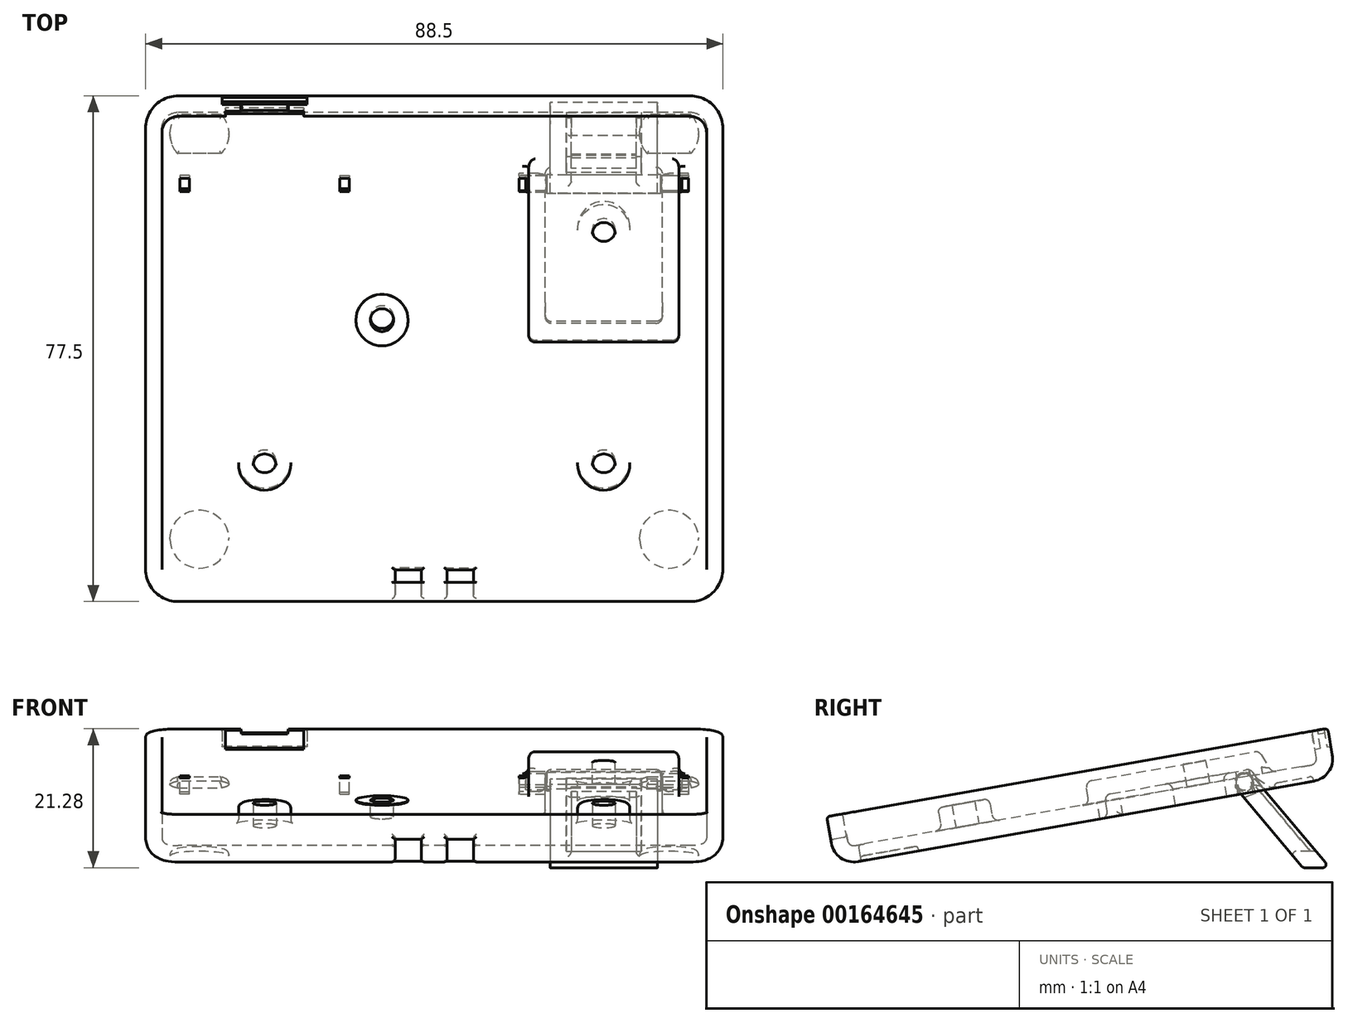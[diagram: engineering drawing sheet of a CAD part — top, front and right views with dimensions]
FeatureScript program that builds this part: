
annotation { "Feature Type Name" : "Feature", "Feature Type Description" : "" }
export const myFeature = defineFeature(function(context is Context, id is Id, definition is map)
    precondition{}
    {
        {
            var Q0;
            Q0=qCreatedBy(makeId("Top.planeOp"),FACE);
            var sketch = newSketch(context, id + "F0", { "sketchPlane" : qUnion([Q0])});
            skLineSegment(sketch, "E0.bottom", {"start": v(-44.25, 39) * mm, "end": v(44.25, 39) * mm});
            skLineSegment(sketch, "E0.top", {"start": v(-44.25, -39) * mm, "end": v(44.25, -39) * mm});
            skLineSegment(sketch, "E0.left", {"start": v(-44.25, 39) * mm, "end": v(-44.25, -39) * mm});
            skLineSegment(sketch, "E0.right", {"start": v(44.25, 39) * mm, "end": v(44.25, -39) * mm});
            skPoint(sketch, "E1", {"position": v(0, -39) * mm});
            skSolve(sketch);
        }
        {
            var Q0;
            Q0=qSketchRegion(id+"F0",true);
            extrude(context, id + "F1", {"entities" : qUnion([Q0]), "depth" : 7.6 * mm});
        }
        {
            var Q0;
            Q0=makeQuery(id+"F1.opExtrude","SWEPT_EDGE",EDGE,{"disambiguationData":[OSD([sQuery(id+"F0.wireOp",EDGE,"E0.top"),sQuery(id+"F0.wireOp",EDGE,"E0.left")])]});
            var Q1;
            Q1=makeQuery(id+"F1.opExtrude","SWEPT_EDGE",EDGE,{"disambiguationData":[OSD([sQuery(id+"F0.wireOp",EDGE,"E0.bottom"),sQuery(id+"F0.wireOp",EDGE,"E0.left")])]});
            var Q2;
            Q2=makeQuery(id+"F1.opExtrude","SWEPT_EDGE",EDGE,{"disambiguationData":[OSD([sQuery(id+"F0.wireOp",EDGE,"E0.top"),sQuery(id+"F0.wireOp",EDGE,"E0.right")])]});
            var Q3;
            Q3=makeQuery(id+"F1.opExtrude","SWEPT_EDGE",EDGE,{"disambiguationData":[OSD([sQuery(id+"F0.wireOp",EDGE,"E0.bottom"),sQuery(id+"F0.wireOp",EDGE,"E0.right")])]});
            fillet(context, id + "F2", {"entities" : qUnion([Q0, Q1, Q2, Q3]), "radius" : 5 * mm, "tangentPropagation" : true, "allowEdgeOverflow" : false});
        }
        {
            assignVariable(context, id + "F3", {"name" : "Thickness", "anyValue" : 2.5});
        }
        {
            var Q0;
            Q0=makeQuery(id+"F1.opExtrude","CAP_FACE",FACE,{"disambiguationData":[OSD([sQuery(id+"F0.wireOp",EDGE,"E0.bottom"),sQuery(id+"F0.wireOp",EDGE,"E0.top"),sQuery(id+"F0.wireOp",EDGE,"E0.left"),sQuery(id+"F0.wireOp",EDGE,"E0.right")])],"isStart":false});
            shell(context, id + "F4", {"entities" : qUnion([Q0]), "thickness" : (getVariable(context, 'Thickness')) * mm});
        }
        {
            var Q0;
            Q0=makeQuery(id+"F4.opShell","OFFSET_FACE",FACE,{"disambiguationData":[OSD([sQuery(id+"F0.wireOp",EDGE,"E0.bottom"),sQuery(id+"F0.wireOp",EDGE,"E0.top"),sQuery(id+"F0.wireOp",EDGE,"E0.left"),sQuery(id+"F0.wireOp",EDGE,"E0.right")])]});
            var sketch = newSketch(context, id + "F5", { "sketchPlane" : qUnion([Q0])});
            skCircle(sketch, "E2", {"center": v(-26, -18) * mm, "radius": 4 * mm});
            skCircle(sketch, "E3.0.1.0", {"center": v(-26, 18) * mm, "radius": 4 * mm, "construction": true});
            skCircle(sketch, "E3.1.0.0", {"center": v(26, -18) * mm, "radius": 4 * mm});
            skCircle(sketch, "E3.1.1.0", {"center": v(26, 18) * mm, "radius": 4 * mm, "construction": true});
            skLineSegment(sketch, "E3.direction1", {"start": v(-26, -18) * mm, "end": v(26, -18) * mm, "construction": true});
            skLineSegment(sketch, "E3.direction2", {"start": v(-26, -18) * mm, "end": v(-26, 18) * mm, "construction": true});
            skSolve(sketch);
        }
        {
            var Q0;
            Q0=qSketchRegion(id+"F5",true);
            extrude(context, id + "F6", {"entities" : qUnion([Q0]), "operationType" : NewBodyOperationType.ADD, "depth" : 3.5 * mm});
        }
        {
            var Q0;
            Q0=makeQuery(id+"F5.imprint","IMPRINT",FACE,{"disambiguationData":[TD([[makeQuery(id+"F5.imprint","IMPRINT",EDGE,{"derivedFrom":sQuery(id+"F5.wireOp",EDGE,"E2")}),-1.0]])]});
            var sketch = newSketch(context, id + "F7", { "sketchPlane" : qUnion([Q0])});
            skCircle(sketch, "E4", {"center": v(-26, -18) * mm, "radius": 1.77 * mm});
            skCircle(sketch, "E5.0.1.0", {"center": v(-26, 18) * mm, "radius": 1.77 * mm});
            skCircle(sketch, "E5.1.0.0", {"center": v(26, -18) * mm, "radius": 1.77 * mm});
            skCircle(sketch, "E5.1.1.0", {"center": v(26, 18) * mm, "radius": 1.77 * mm});
            skLineSegment(sketch, "E5.direction1", {"start": v(-26, -18) * mm, "end": v(26, -18) * mm, "construction": true});
            skLineSegment(sketch, "E5.direction2", {"start": v(-26, -18) * mm, "end": v(-26, 18) * mm, "construction": true});
            skSolve(sketch);
        }
        {
            var Q0;
            Q0=qSketchRegion(id+"F7",true);
            extrude(context, id + "F8", {"entities" : qUnion([Q0]), "operationType" : NewBodyOperationType.REMOVE, "depth" : 25 * mm});
        }
        {
            var Q0;
            Q0=makeQuery(id+"F6.opExtrude","CAP_EDGE",EDGE,{"disambiguationData":[OSD([sQuery(id+"F5.wireOp",EDGE,"E3.0.1.0")])],"isStart":false});
            var Q1;
            Q1=makeQuery(id+"F6.opExtrude","CAP_EDGE",EDGE,{"disambiguationData":[OSD([sQuery(id+"F5.wireOp",EDGE,"E2")])],"isStart":false});
            var Q2;
            Q2=makeQuery(id+"F6.opExtrude","CAP_EDGE",EDGE,{"disambiguationData":[OSD([sQuery(id+"F5.wireOp",EDGE,"E3.1.1.0")])],"isStart":false});
            var Q3;
            Q3=makeQuery(id+"F6.opExtrude","CAP_EDGE",EDGE,{"disambiguationData":[OSD([sQuery(id+"F5.wireOp",EDGE,"E3.1.0.0")])],"isStart":false});
            fillet(context, id + "F9", {"entities" : qUnion([Q0, Q1, Q2, Q3]), "radius" : 0.8 * mm, "tangentPropagation" : true, "allowEdgeOverflow" : false});
        }
        {
            var Q0;
            Q0=makeQuery(id+"F4.opShell","OFFSET_FACE",FACE,{"disambiguationData":[OSD([sQuery(id+"F0.wireOp",EDGE,"E0.bottom"),sQuery(id+"F0.wireOp",EDGE,"E0.top"),sQuery(id+"F0.wireOp",EDGE,"E0.left"),sQuery(id+"F0.wireOp",EDGE,"E0.right")])]});
            fillet(context, id + "F10", {"entities" : qUnion([Q0]), "radius" : 1 * mm, "tangentPropagation" : true, "allowEdgeOverflow" : false});
        }
        {
            var Q0;
            Q0=makeQuery(id+"F1.opExtrude","CAP_FACE",FACE,{"disambiguationData":[OSD([sQuery(id+"F0.wireOp",EDGE,"E0.bottom"),sQuery(id+"F0.wireOp",EDGE,"E0.top"),sQuery(id+"F0.wireOp",EDGE,"E0.left"),sQuery(id+"F0.wireOp",EDGE,"E0.right")])],"isStart":true});
            fillet(context, id + "F11", {"entities" : qUnion([Q0]), "radius" : 3.5 * mm, "tangentPropagation" : true, "allowEdgeOverflow" : false});
        }
        {
            var Q0;
            Q0=makeQuery(id+"F1.opExtrude","CAP_FACE",FACE,{"disambiguationData":[OSD([sQuery(id+"F0.wireOp",EDGE,"E0.bottom"),sQuery(id+"F0.wireOp",EDGE,"E0.top"),sQuery(id+"F0.wireOp",EDGE,"E0.left"),sQuery(id+"F0.wireOp",EDGE,"E0.right")])],"isStart":true});
            var sketch = newSketch(context, id + "F12", { "sketchPlane" : qUnion([Q0])});
            skLineSegment(sketch, "E6", {"start": v(0, 29.34) * mm, "end": v(0, 8.5) * mm, "construction": true});
            skCircle(sketch, "E7", {"center": v(-36, 30.5) * mm, "radius": 4.5 * mm});
            skCircle(sketch, "E8.MirrorC", {"center": v(36, 30.5) * mm, "radius": 4.5 * mm});
            skLineSegment(sketch, "E9.direction1", {"start": v(-36, 30.5) * mm, "end": v(-15, 30.5) * mm, "construction": true});
            skCircle(sketch, "E10.0.1.0", {"center": v(-36, -32.5) * mm, "radius": 4.5 * mm, "construction": true});
            skLineSegment(sketch, "E10.direction2", {"start": v(-36, 30.5) * mm, "end": v(-36, -32.5) * mm, "construction": true});
            skCircle(sketch, "E11.0.1.0", {"center": v(36, -33.5) * mm, "radius": 4.5 * mm, "construction": true});
            skLineSegment(sketch, "E11.direction1", {"start": v(36, 30.5) * mm, "end": v(61, 30.5) * mm, "construction": true});
            skLineSegment(sketch, "E11.direction2", {"start": v(36, 30.5) * mm, "end": v(36, -33.5) * mm, "construction": true});
            skLineSegment(sketch, "E12", {"start": v(-39.35, -29.5) * mm, "end": v(-32.65, -29.5) * mm});
            skLineSegment(sketch, "E13", {"start": v(-32.65, -35.5) * mm, "end": v(-39.35, -35.5) * mm});
            skLineSegment(sketch, "E14", {"start": v(-36.31, -32.5) * mm, "end": v(-36, -32.5) * mm, "construction": true});
            skArc(sketch, "E15", {"start": v(-32.65, -35.5) * mm, "mid": v(-31.5, -32.5) * mm, "end": v(-32.65, -29.5) * mm});
            skArc(sketch, "E16", {"start": v(-39.35, -29.5) * mm, "mid": v(-40.5, -32.5) * mm, "end": v(-39.35, -35.5) * mm});
            skLineSegment(sketch, "E17.1.0.0", {"start": v(39.35, -35.5) * mm, "end": v(32.65, -35.5) * mm});
            skArc(sketch, "E17.1.0.1", {"start": v(39.35, -35.5) * mm, "mid": v(40.5, -32.5) * mm, "end": v(39.35, -29.5) * mm});
            skArc(sketch, "E17.1.0.2", {"start": v(32.65, -29.5) * mm, "mid": v(31.5, -32.5) * mm, "end": v(32.65, -35.5) * mm});
            skLineSegment(sketch, "E17.1.0.3", {"start": v(32.65, -29.5) * mm, "end": v(39.35, -29.5) * mm});
            skLineSegment(sketch, "E17.direction1", {"start": v(-39.35, -35.5) * mm, "end": v(32.65, -35.5) * mm, "construction": true});
            skSolve(sketch);
        }
        {
            var Q0;
            Q0=makeQuery(id+"F1.opExtrude","CAP_FACE",FACE,{"disambiguationData":[OSD([sQuery(id+"F0.wireOp",EDGE,"E0.bottom"),sQuery(id+"F0.wireOp",EDGE,"E0.top"),sQuery(id+"F0.wireOp",EDGE,"E0.left"),sQuery(id+"F0.wireOp",EDGE,"E0.right")])],"isStart":false});
            fillet(context, id + "F13", {"entities" : qUnion([Q0]), "radius" : 0.5 * mm, "tangentPropagation" : true, "allowEdgeOverflow" : false});
        }
        {
            var Q0;
            Q0=qCreatedBy(makeId("Top.planeOp"),FACE);
            var sketch = newSketch(context, id + "F14", { "sketchPlane" : qUnion([Q0])});
            skLineSegment(sketch, "E18", {"start": v(-15.25, 0) * mm, "end": v(18.86, 0) * mm});
            skSolve(sketch);
        }
        {
            assignVariable(context, id + "F15", {"name" : "FootWidth", "anyValue" : 23});
        }
        {
            var Q0;
            Q0=qCreatedBy(makeId("Right.planeOp"),FACE);
            cPlane(context, id + "F16", {"entities" : qUnion([Q0]), "cplaneType" : CPlaneType.OFFSET, "offset" : 26 * mm, "width" : 150 * mm, "height" : 150 * mm});
        }
        {
            var Q0;
            Q0=qCreatedBy(id+"F16.planeOp",FACE);
            var sketch = newSketch(context, id + "F17", { "sketchPlane" : qUnion([Q0])});
            skLineSegment(sketch, "E19", {"start": v(1, 6) * mm, "end": v(28, 6) * mm});
            skLineSegment(sketch, "E20", {"start": v(28, 6) * mm, "end": v(30.42, 0) * mm});
            skLineSegment(sketch, "E21", {"start": v(30.42, 0) * mm, "end": v(1, 0) * mm});
            skLineSegment(sketch, "E22", {"start": v(1, 0) * mm, "end": v(1, 6) * mm});
            skSolve(sketch);
        }
        {
            var Q0;
            Q0=qSketchRegion(id+"F17",true);
            extrude(context, id + "F18", {"entities" : qUnion([Q0]), "operationType" : NewBodyOperationType.ADD, "endBound" : BoundingType.SYMMETRIC, "depth" : (getVariable(context, 'FootWidth')) * mm});
        }
        {
            var Q0;
            Q0=qCreatedBy(id+"F16.planeOp",FACE);
            var sketch = newSketch(context, id + "F19", { "sketchPlane" : qUnion([Q0])});
            skLineSegment(sketch, "E23.0", {"start": v(26.31, 3.5) * mm, "end": v(27.73, 0) * mm});
            skLineSegment(sketch, "E23.1", {"start": v(3.5, 3.5) * mm, "end": v(26.31, 3.5) * mm});
            skLineSegment(sketch, "E23.2", {"start": v(3.5, 0) * mm, "end": v(3.5, 3.5) * mm});
            skLineSegment(sketch, "E24", {"start": v(3.5, 0) * mm, "end": v(27.73, 0) * mm});
            skSolve(sketch);
        }
        {
            var Q0;
            Q0=qSketchRegion(id+"F19",true);
            extrude(context, id + "F20", {"entities" : qUnion([Q0]), "operationType" : NewBodyOperationType.REMOVE, "endBound" : BoundingType.SYMMETRIC, "oppositeDirection" : true, "depth" : (getVariable(context, 'FootWidth') - 2.5 * 2) * mm});
        }
        {
            var Q0;
            Q0=qSketchRegion(id+"F12",true);
            extrude(context, id + "F21", {"entities" : qUnion([Q0]), "operationType" : NewBodyOperationType.REMOVE, "oppositeDirection" : true, "depth" : 0.75 * mm});
        }
        {
            var Q0;
            Q0=makeQuery(id+"F21.boolean.opBoolean","COPY",EDGE,{"derivedFrom":makeQuery(id+"F21.opExtrude","CAP_EDGE",EDGE,{"disambiguationData":[OSD([sQuery(id+"F12.wireOp",EDGE,"E7")])],"isStart":false})});
            var Q1;
            Q1=makeQuery(id+"F21.boolean.opBoolean","COPY",EDGE,{"derivedFrom":makeQuery(id+"F21.opExtrude","CAP_EDGE",EDGE,{"disambiguationData":[OSD([sQuery(id+"F12.wireOp",EDGE,"E8.MirrorC")])],"isStart":false})});
            var Q2;
            Q2=makeQuery(id+"F21.boolean.opBoolean","COPY",EDGE,{"derivedFrom":makeQuery(id+"F21.opExtrude","CAP_EDGE",EDGE,{"disambiguationData":[OSD([sQuery(id+"F12.wireOp",EDGE,"E16")])],"isStart":false})});
            var Q3;
            Q3=makeQuery(id+"F21.boolean.opBoolean","COPY",EDGE,{"derivedFrom":makeQuery(id+"F21.opExtrude","CAP_EDGE",EDGE,{"disambiguationData":[OSD([sQuery(id+"F12.wireOp",EDGE,"E12")])],"isStart":false})});
            var Q4;
            Q4=makeQuery(id+"F21.boolean.opBoolean","COPY",EDGE,{"derivedFrom":makeQuery(id+"F21.opExtrude","CAP_EDGE",EDGE,{"disambiguationData":[OSD([sQuery(id+"F12.wireOp",EDGE,"E15")])],"isStart":false})});
            var Q5;
            Q5=makeQuery(id+"F21.boolean.opBoolean","COPY",EDGE,{"derivedFrom":makeQuery(id+"F21.opExtrude","CAP_EDGE",EDGE,{"disambiguationData":[OSD([sQuery(id+"F12.wireOp",EDGE,"E13")])],"isStart":false})});
            var Q6;
            Q6=makeQuery(id+"F21.boolean.opBoolean","COPY",EDGE,{"derivedFrom":makeQuery(id+"F21.opExtrude","CAP_EDGE",EDGE,{"disambiguationData":[OSD([sQuery(id+"F12.wireOp",EDGE,"E17.1.0.2")])],"isStart":false})});
            var Q7;
            Q7=makeQuery(id+"F21.boolean.opBoolean","COPY",EDGE,{"derivedFrom":makeQuery(id+"F21.opExtrude","CAP_EDGE",EDGE,{"disambiguationData":[OSD([sQuery(id+"F12.wireOp",EDGE,"E17.1.0.3")])],"isStart":false})});
            var Q8;
            Q8=makeQuery(id+"F21.boolean.opBoolean","COPY",EDGE,{"derivedFrom":makeQuery(id+"F21.opExtrude","CAP_EDGE",EDGE,{"disambiguationData":[OSD([sQuery(id+"F12.wireOp",EDGE,"E17.1.0.1")])],"isStart":false})});
            var Q9;
            Q9=makeQuery(id+"F21.boolean.opBoolean","COPY",EDGE,{"derivedFrom":makeQuery(id+"F21.opExtrude","CAP_EDGE",EDGE,{"disambiguationData":[OSD([sQuery(id+"F12.wireOp",EDGE,"E17.1.0.0")])],"isStart":false})});
            fillet(context, id + "F22", {"entities" : qUnion([Q0, Q1, Q2, Q3, Q4, Q5, Q6, Q7, Q8, Q9]), "radius" : 0.5 * mm, "tangentPropagation" : true, "allowEdgeOverflow" : false});
        }
        {
            var Q0;
            Q0=makeQuery(id+"F9l8tkFQPLfUdVu_1.1.F18.opExtrude","SWEPT_FACE",FACE,{"disambiguationData":[OSD([sQuery(id+"F17.wireOp",EDGE,"E19")])]});
            var Q1;
            Q1=makeQuery(id+"F9l8tkFQPLfUdVu_1.1.F20.boolean.opBoolean","COPY",FACE,{"derivedFrom":makeQuery(id+"F9l8tkFQPLfUdVu_1.1.F20.opExtrude","SWEPT_FACE",FACE,{"disambiguationData":[OSD([sQuery(id+"F19.wireOp",EDGE,"E23.1")])]})});
            var Q2;
            Q2=makeQuery(id+"F20.boolean.opBoolean","COPY",FACE,{"derivedFrom":makeQuery(id+"F20.opExtrude","SWEPT_FACE",FACE,{"disambiguationData":[OSD([sQuery(id+"F19.wireOp",EDGE,"E23.1")])]})});
            var Q3;
            Q3=makeQuery(id+"F9l8tkFQPLfUdVu_1.1.F18.opExtrude","SWEPT_FACE",FACE,{"disambiguationData":[OSD([sQuery(id+"F17.wireOp",EDGE,"E22")])]});
            var Q4;
            Q4=makeQuery(id+"F9l8tkFQPLfUdVu_1.1.F18.opExtrude","SWEPT_FACE",FACE,{"disambiguationData":[OSD([sQuery(id+"F17.wireOp",EDGE,"E20")])]});
            var Q5;
            Q5=makeQuery(id+"F18.opExtrude","SWEPT_FACE",FACE,{"disambiguationData":[OSD([sQuery(id+"F17.wireOp",EDGE,"E22")])]});
            var Q6;
            Q6=makeQuery(id+"F18.opExtrude","SWEPT_FACE",FACE,{"disambiguationData":[OSD([sQuery(id+"F17.wireOp",EDGE,"E20")])]});
            var Q7;
            Q7=makeQuery(id+"F9l8tkFQPLfUdVu_1.1.F20.boolean.opBoolean","COPY",FACE,{"derivedFrom":makeQuery(id+"F9l8tkFQPLfUdVu_1.1.F20.opExtrude","SWEPT_FACE",FACE,{"disambiguationData":[OSD([sQuery(id+"F19.wireOp",EDGE,"E23.2")])]})});
            var Q8;
            Q8=makeQuery(id+"F9l8tkFQPLfUdVu_1.1.F20.boolean.opBoolean","COPY",FACE,{"derivedFrom":makeQuery(id+"F9l8tkFQPLfUdVu_1.1.F20.opExtrude","SWEPT_FACE",FACE,{"disambiguationData":[OSD([sQuery(id+"F19.wireOp",EDGE,"E23.0")])]})});
            var Q9;
            Q9=makeQuery(id+"F20.boolean.opBoolean","COPY",FACE,{"derivedFrom":makeQuery(id+"F20.opExtrude","SWEPT_FACE",FACE,{"disambiguationData":[OSD([sQuery(id+"F19.wireOp",EDGE,"E23.2")])]})});
            var Q10;
            Q10=makeQuery(id+"F20.boolean.opBoolean","COPY",FACE,{"derivedFrom":makeQuery(id+"F20.opExtrude","SWEPT_FACE",FACE,{"disambiguationData":[OSD([sQuery(id+"F19.wireOp",EDGE,"E23.0")])]})});
            var Q11;
            Q11=makeQuery(id+"F18.opExtrude","CAP_FACE",FACE,{"disambiguationData":[OSD([sQuery(id+"F17.wireOp",EDGE,"E19"),sQuery(id+"F17.wireOp",EDGE,"E20"),sQuery(id+"F17.wireOp",EDGE,"E21"),sQuery(id+"F17.wireOp",EDGE,"E22")])],"isStart":false});
            var Q12;
            Q12=makeQuery(id+"F18.opExtrude","CAP_FACE",FACE,{"disambiguationData":[OSD([sQuery(id+"F17.wireOp",EDGE,"E19"),sQuery(id+"F17.wireOp",EDGE,"E20"),sQuery(id+"F17.wireOp",EDGE,"E21"),sQuery(id+"F17.wireOp",EDGE,"E22")])],"isStart":true});
            fillet(context, id + "F23", {"entities" : qUnion([Q0, Q1, Q2, Q3, Q4, Q5, Q6, Q7, Q8, Q9, Q10, Q11, Q12]), "radius" : 1 * mm, "tangentPropagation" : true, "allowEdgeOverflow" : false});
        }
        {
            var Q0;
            Q0=makeQuery(id+"F18.opExtrude","SWEPT_FACE",FACE,{"disambiguationData":[OSD([sQuery(id+"F17.wireOp",EDGE,"E19")])]});
            var sketch = newSketch(context, id + "F24", { "sketchPlane" : qUnion([Q0])});
            skCircle(sketch, "E25.0", {"center": v(26, 18) * mm, "radius": 4 * mm});
            skSolve(sketch);
        }
        {
            var Q0;
            Q0=qSketchRegion(id+"F24",true);
            var Q1;
            Q1=makeQuery(id+"F1.opExtrude","CAP_FACE",FACE,{"disambiguationData":[OSD([sQuery(id+"F0.wireOp",EDGE,"E0.bottom"),sQuery(id+"F0.wireOp",EDGE,"E0.top"),sQuery(id+"F0.wireOp",EDGE,"E0.left"),sQuery(id+"F0.wireOp",EDGE,"E0.right")])],"isStart":true});
            extrude(context, id + "F25", {"entities" : qUnion([Q0]), "operationType" : NewBodyOperationType.ADD, "endBound" : BoundingType.UP_TO_SURFACE, "oppositeDirection" : true, "endBoundEntityFace" : qUnion([Q1]), "depth" : 25 * mm});
        }
        {
            var Q0;
            Q0=makeQuery(id+"F18.opExtrude","SWEPT_FACE",FACE,{"disambiguationData":[OSD([sQuery(id+"F17.wireOp",EDGE,"E19")])]});
            var sketch = newSketch(context, id + "F26", { "sketchPlane" : qUnion([Q0])});
            skCircle(sketch, "E26.0", {"center": v(26, 18) * mm, "radius": 1.77 * mm});
            skSolve(sketch);
        }
        {
            var Q0;
            Q0=qSketchRegion(id+"F26",true);
            extrude(context, id + "F27", {"entities" : qUnion([Q0]), "operationType" : NewBodyOperationType.REMOVE, "oppositeDirection" : true, "depth" : 3.5 * mm});
        }
        {
            var Q0;
            Q0=makeQuery(id+"F25.opExtrude","TWEAK_EDGE",EDGE,{"derivedFrom":[makeQuery(id+"F1.opExtrude","CAP_FACE",FACE,{"disambiguationData":[OSD([sQuery(id+"F0.wireOp",EDGE,"E0.bottom"),sQuery(id+"F0.wireOp",EDGE,"E0.top"),sQuery(id+"F0.wireOp",EDGE,"E0.left"),sQuery(id+"F0.wireOp",EDGE,"E0.right")])],"isStart":true}),makeQuery(id+"F24.imprint","IMPRINT",EDGE,{"derivedFrom":sQuery(id+"F24.wireOp",EDGE,"E25.0")})]});
            var Q1;
            Q1=makeQuery(id+"F25.boolean.opBoolean","INTERSECT",EDGE,{"derivedFrom":[makeQuery(id+"F20.boolean.opBoolean","COPY",FACE,{"derivedFrom":makeQuery(id+"F20.opExtrude","SWEPT_FACE",FACE,{"disambiguationData":[OSD([sQuery(id+"F19.wireOp",EDGE,"E23.1")])]})}),makeQuery(id+"F25.opExtrude","SWEPT_FACE",FACE,{"disambiguationData":[OSD([sQuery(id+"F24.wireOp",EDGE,"E25.0")])]})]});
            fillet(context, id + "F28", {"entities" : qUnion([Q0, Q1]), "radius" : 1 * mm, "tangentPropagation" : true, "allowEdgeOverflow" : false});
        }
        {
            var Q0;
            Q0=qCreatedBy(id+"F16.planeOp",FACE);
            var sketch = newSketch(context, id + "F29", { "sketchPlane" : qUnion([Q0])});
            skArc(sketch, "E27", {"start": v(26.22, 1.25) * mm, "mid": v(25, 3) * mm, "end": v(23.78, 1.25) * mm});
            skLineSegment(sketch, "E28", {"start": v(23.65, 0) * mm, "end": v(26.35, 0) * mm});
            skLineSegment(sketch, "E29", {"start": v(23.78, 1.25) * mm, "end": v(23.85, 1.06) * mm});
            skLineSegment(sketch, "E30", {"start": v(23.85, 1.06) * mm, "end": v(23.65, 0) * mm});
            skLineSegment(sketch, "E31", {"start": v(26.22, 1.25) * mm, "end": v(26.15, 1.06) * mm});
            skLineSegment(sketch, "E32", {"start": v(26.15, 1.06) * mm, "end": v(26.35, 0) * mm});
            skLineSegment(sketch, "E33", {"start": v(25, 1.7) * mm, "end": v(25, 0.9) * mm, "construction": true});
            skPoint(sketch, "E34.0", {"position": v(1, 0) * mm});
            skSolve(sketch);
        }
        {
            var Q0;
            Q0=qSketchRegion(id+"F29",true);
            extrude(context, id + "F30", {"entities" : qUnion([Q0]), "operationType" : NewBodyOperationType.REMOVE, "endBound" : BoundingType.SYMMETRIC, "depth" : (getVariable(context, 'FootWidth') + 3) * mm});
        }
        {
            var Q0;
            Q0=makeQuery(id+"F1.opExtrude","SWEPT_BODY",BODY,{"disambiguationData":[OSD([sQuery(id+"F0.wireOp",EDGE,"E0.bottom"),sQuery(id+"F0.wireOp",EDGE,"E0.top"),sQuery(id+"F0.wireOp",EDGE,"E0.left"),sQuery(id+"F0.wireOp",EDGE,"E0.right")])]});
            var Q1;
            Q1=sQuery(id+"F14.wireOp",EDGE,"E18");
            transform(context, id + "F31", {"entities" : qUnion([Q0]), "transformType" : TransformType.ROTATION, "transformAxis" : qUnion([Q1]), "angle" : 10 * degree, "makeCopy" : false});
        }
        {
            var Q0;
            Q0=qCreatedBy(id+"F16.planeOp",FACE);
            var sketch = newSketch(context, id + "F32", { "sketchPlane" : qUnion([Q0])});
            skLineSegment(sketch, "E35", {"start": v(-33.48, -7.1) * mm, "end": v(29.13, -7.1) * mm, "construction": true});
            skLineSegment(sketch, "E36", {"start": v(29.13, -7.1) * mm, "end": v(29.13, 7.53) * mm, "construction": true});
            skLineSegment(sketch, "E37", {"start": v(23.12, 5.69) * mm, "end": v(25.51, 6.42) * mm});
            skCircle(sketch, "E38", {"center": v(24.32, 6.06) * mm, "radius": 1.25 * mm, "construction": true});
            skLineSegment(sketch, "E39.0", {"start": v(-26.23, -3.86) * mm, "end": v(-34.1, -5.25) * mm, "construction": true});
            skLineSegment(sketch, "E40.0", {"start": v(-27.36, -6.1) * mm, "end": v(-35.24, -7.48) * mm, "construction": true});
            skLineSegment(sketch, "E41", {"start": v(22.63, 5.54) * mm, "end": v(33.3, -7.1) * mm});
            skLineSegment(sketch, "E42", {"start": v(25.9, 6.54) * mm, "end": v(37.42, -7.1) * mm});
            skLineSegment(sketch, "E43", {"start": v(22.63, 5.54) * mm, "end": v(23.12, 5.69) * mm});
            skLineSegment(sketch, "E44", {"start": v(25.9, 6.54) * mm, "end": v(25.51, 6.42) * mm});
            skLineSegment(sketch, "E45", {"start": v(37.42, -7.1) * mm, "end": v(33.3, -7.1) * mm});
            skArc(sketch, "E46.0", {"start": v(28.3, 7.6) * mm, "mid": v(28.39, 7.4) * mm, "end": v(28.45, 7.19) * mm});
            skSolve(sketch);
        }
        {
            var Q0;
            Q0=qSketchRegion(id+"F32",true);
            extrude(context, id + "F33", {"entities" : qUnion([Q0]), "endBound" : BoundingType.SYMMETRIC, "depth" : 16.5 * mm});
        }
        {
            var Q0;
            Q0=qCreatedBy(id+"F16.planeOp",FACE);
            var sketch = newSketch(context, id + "F34", { "sketchPlane" : qUnion([Q0])});
            skCircle(sketch, "E47.0", {"center": v(24.32, 6.06) * mm, "radius": 1.25 * mm});
            skSolve(sketch);
        }
        {
            var Q0;
            Q0=makeQuery(id+"F4.opShell","OFFSET_FACE",FACE,{"disambiguationData":[OSD([sQuery(id+"F0.wireOp",EDGE,"E0.bottom"),sQuery(id+"F0.wireOp",EDGE,"E0.top"),sQuery(id+"F0.wireOp",EDGE,"E0.left"),sQuery(id+"F0.wireOp",EDGE,"E0.right")])]});
            var sketch = newSketch(context, id + "F35", { "sketchPlane" : qUnion([Q0])});
            skLineSegment(sketch, "E48.bottom", {"start": v(-39, 26.02) * mm, "end": v(-37.5, 26.02) * mm});
            skLineSegment(sketch, "E48.top", {"start": v(-39, 23.98) * mm, "end": v(-37.5, 23.98) * mm});
            skLineSegment(sketch, "E48.left", {"start": v(-39, 26.02) * mm, "end": v(-39, 23.98) * mm});
            skLineSegment(sketch, "E48.right", {"start": v(-37.5, 26.02) * mm, "end": v(-37.5, 23.98) * mm});
            skLineSegment(sketch, "E49.MirrorCS", {"start": v(-13, 23.98) * mm, "end": v(-14.5, 23.98) * mm});
            skLineSegment(sketch, "E50.MirrorCS", {"start": v(-13, 26.02) * mm, "end": v(-14.5, 26.02) * mm});
            skLineSegment(sketch, "E51.MirrorCS", {"start": v(-13, 26.02) * mm, "end": v(-13, 23.98) * mm});
            skLineSegment(sketch, "E52.MirrorCS", {"start": v(-14.5, 26.02) * mm, "end": v(-14.5, 23.98) * mm});
            skLineSegment(sketch, "E53", {"start": v(0, 27.5) * mm, "end": v(0, 11.46) * mm, "construction": true});
            skLineSegment(sketch, "E54.MirrorCS", {"start": v(39, 26.02) * mm, "end": v(37.5, 26.02) * mm});
            skLineSegment(sketch, "E55.MirrorCS", {"start": v(39, 23.98) * mm, "end": v(37.5, 23.98) * mm});
            skLineSegment(sketch, "E56.MirrorCS", {"start": v(13, 26.02) * mm, "end": v(14.5, 26.02) * mm});
            skLineSegment(sketch, "E57.MirrorCS", {"start": v(13, 23.98) * mm, "end": v(14.5, 23.98) * mm});
            skLineSegment(sketch, "E58.MirrorCS", {"start": v(14.5, 26.02) * mm, "end": v(14.5, 23.98) * mm});
            skLineSegment(sketch, "E59.MirrorCS", {"start": v(39, 26.02) * mm, "end": v(39, 23.98) * mm});
            skLineSegment(sketch, "E60.MirrorCS", {"start": v(13, 26.02) * mm, "end": v(13, 23.98) * mm});
            skLineSegment(sketch, "E61.MirrorCS", {"start": v(37.5, 26.02) * mm, "end": v(37.5, 23.98) * mm});
            skSolve(sketch);
        }
        {
            var Q0;
            Q0=qSketchRegion(id+"F35",true);
            var Q1;
            Q1=makeQuery(id+"F1.opExtrude","CAP_FACE",FACE,{"disambiguationData":[OSD([sQuery(id+"F0.wireOp",EDGE,"E0.bottom"),sQuery(id+"F0.wireOp",EDGE,"E0.top"),sQuery(id+"F0.wireOp",EDGE,"E0.left"),sQuery(id+"F0.wireOp",EDGE,"E0.right")])],"isStart":true});
            extrude(context, id + "F36", {"entities" : qUnion([Q0]), "operationType" : NewBodyOperationType.REMOVE, "endBound" : BoundingType.UP_TO_SURFACE, "oppositeDirection" : true, "endBoundEntityFace" : qUnion([Q1]), "depth" : 25 * mm, "hasSecondDirection" : true, "secondDirectionOppositeDirection" : false, "secondDirectionDepth" : 25 * mm});
        }
        {
            var Q0;
            Q0=qSketchRegion(id+"F34",true);
            extrude(context, id + "F37", {"entities" : qUnion([Q0]), "operationType" : NewBodyOperationType.ADD, "endBound" : BoundingType.SYMMETRIC, "depth" : 24 * mm});
        }
        {
            var Q0;
            Q0=qCreatedBy(id+"F16.planeOp",FACE);
            var sketch = newSketch(context, id + "F38", { "sketchPlane" : qUnion([Q0])});
            skCircle(sketch, "E62.0", {"center": v(24.32, 6.06) * mm, "radius": 1.45 * mm});
            skSolve(sketch);
        }
        {
            var Q0;
            Q0=qSketchRegion(id+"F38",true);
            extrude(context, id + "F39", {"entities" : qUnion([Q0]), "operationType" : NewBodyOperationType.ADD, "endBound" : BoundingType.SYMMETRIC, "depth" : 17.5 * mm});
        }
        {
            var Q0;
            Q0=qCreatedBy(id+"F16.planeOp",FACE);
            var sketch = newSketch(context, id + "F40", { "sketchPlane" : qUnion([Q0])});
            skLineSegment(sketch, "E63", {"start": v(43.2, -4.6) * mm, "end": v(34.46, -4.6) * mm});
            skLineSegment(sketch, "E64", {"start": v(34.46, -4.6) * mm, "end": v(25.79, 5.68) * mm});
            skLineSegment(sketch, "E65", {"start": v(25.79, 5.68) * mm, "end": v(25.67, 6.98) * mm});
            skLineSegment(sketch, "E66", {"start": v(25.67, 6.98) * mm, "end": v(43.2, -4.6) * mm});
            skSolve(sketch);
        }
        {
            var Q0;
            Q0=qSketchRegion(id+"F40",true);
            extrude(context, id + "F41", {"entities" : qUnion([Q0]), "operationType" : NewBodyOperationType.REMOVE, "endBound" : BoundingType.SYMMETRIC, "oppositeDirection" : true, "depth" : (16.5 - 2.5 * 2) * mm});
        }
        {
            var Q0;
            Q0=qCreatedBy(makeId("Top.planeOp"),FACE);
            var Q1;
            Q1=sQuery(id+"F32.wireOp",VERTEX,"E38.center");
            cPlane(context, id + "F42", {"entities" : qUnion([Q0, Q1]), "cplaneType" : CPlaneType.PLANE_POINT, "offset" : 7 * mm, "width" : 150 * mm, "height" : 150 * mm});
        }
        {
            var Q0;
            Q0=qCreatedBy(id+"F42.planeOp",FACE);
            var sketch = newSketch(context, id + "F43", { "sketchPlane" : qUnion([Q0])});
            skLineSegment(sketch, "E67", {"start": v(12.14, 24.32) * mm, "end": v(28.07, 24.32) * mm});
            skSolve(sketch);
        }
        {
            var Q0;
            Q0=qCreatedBy(id+"F16.planeOp",FACE);
            var sketch = newSketch(context, id + "F44", { "sketchPlane" : qUnion([Q0])});
            skLineSegment(sketch, "E68", {"start": v(37.44, -4.6) * mm, "end": v(28.89, -4.6) * mm});
            skLineSegment(sketch, "E69", {"start": v(28.89, -4.6) * mm, "end": v(22.62, 3.07) * mm});
            skLineSegment(sketch, "E70", {"start": v(22.62, 3.07) * mm, "end": v(28.76, 5.3) * mm});
            skLineSegment(sketch, "E71", {"start": v(28.76, 5.3) * mm, "end": v(37.44, -4.6) * mm});
            skSolve(sketch);
        }
        {
            var Q0;
            Q0=qSketchRegion(id+"F44",true);
            extrude(context, id + "F45", {"entities" : qUnion([Q0]), "operationType" : NewBodyOperationType.REMOVE, "endBound" : BoundingType.SYMMETRIC, "oppositeDirection" : true, "depth" : 10 * mm});
        }
        {
            var Q0;
            Q0=makeQuery(id+"F33.opExtrude","SWEPT_EDGE",EDGE,{"disambiguationData":[OSD([sQuery(id+"F32.wireOp",EDGE,"E42"),sQuery(id+"F32.wireOp",EDGE,"lMs646Tl-KVh7-EVDn-IebO-JsbN2g6ax7Xg")])]});
            var Q1;
            Q1=makeQuery(id+"F33.opExtrude","SWEPT_EDGE",EDGE,{"disambiguationData":[OSD([sQuery(id+"F32.wireOp",EDGE,"E41"),sQuery(id+"F32.wireOp",EDGE,"NX3cYOfe-ebx6-K3RK-W4n3-XHnWPqz6DOJI")])]});
            var Q2;
            Q2=makeQuery(id+"F45.boolean.opBoolean","INTERSECT",EDGE,{"derivedFrom":[makeQuery(id+"F33.opExtrude","SWEPT_FACE",FACE,{"disambiguationData":[OSD([sQuery(id+"F32.wireOp",EDGE,"E41")])]}),makeQuery(id+"F45.opExtrude","SWEPT_FACE",FACE,{"disambiguationData":[OSD([sQuery(id+"F44.wireOp",EDGE,"E68")])]})]});
            var Q3;
            Q3=makeQuery(id+"F45.boolean.opBoolean","INTERSECT",EDGE,{"derivedFrom":[makeQuery(id+"F33.opExtrude","SWEPT_FACE",FACE,{"disambiguationData":[OSD([sQuery(id+"F32.wireOp",EDGE,"E41")])]}),makeQuery(id+"F45.opExtrude","CAP_FACE",FACE,{"disambiguationData":[OSD([sQuery(id+"F44.wireOp",EDGE,"E68"),sQuery(id+"F44.wireOp",EDGE,"E69"),sQuery(id+"F44.wireOp",EDGE,"E70"),sQuery(id+"F44.wireOp",EDGE,"E71")])],"isStart":false})]});
            var Q4;
            Q4=makeQuery(id+"F45.boolean.opBoolean","INTERSECT",EDGE,{"derivedFrom":[makeQuery(id+"F33.opExtrude","SWEPT_FACE",FACE,{"disambiguationData":[OSD([sQuery(id+"F32.wireOp",EDGE,"E41")])]}),makeQuery(id+"F45.opExtrude","SWEPT_FACE",FACE,{"disambiguationData":[OSD([sQuery(id+"F44.wireOp",EDGE,"E70")])]})]});
            var Q5;
            Q5=makeQuery(id+"F45.boolean.opBoolean","INTERSECT",EDGE,{"derivedFrom":[makeQuery(id+"F33.opExtrude","SWEPT_FACE",FACE,{"disambiguationData":[OSD([sQuery(id+"F32.wireOp",EDGE,"E41")])]}),makeQuery(id+"F45.opExtrude","CAP_FACE",FACE,{"disambiguationData":[OSD([sQuery(id+"F44.wireOp",EDGE,"E68"),sQuery(id+"F44.wireOp",EDGE,"E69"),sQuery(id+"F44.wireOp",EDGE,"E70"),sQuery(id+"F44.wireOp",EDGE,"E71")])],"isStart":true})]});
            fillet(context, id + "F46", {"entities" : qUnion([Q0, Q1, Q2, Q3, Q4, Q5]), "radius" : 0.5 * mm, "tangentPropagation" : true, "allowEdgeOverflow" : false});
        }
        {
            var Q0;
            Q0=makeQuery(id+"F1.opExtrude","CAP_FACE",FACE,{"disambiguationData":[OSD([sQuery(id+"F0.wireOp",EDGE,"E0.bottom"),sQuery(id+"F0.wireOp",EDGE,"E0.top"),sQuery(id+"F0.wireOp",EDGE,"E0.left"),sQuery(id+"F0.wireOp",EDGE,"E0.right")])],"isStart":true});
            var sketch = newSketch(context, id + "F47", { "sketchPlane" : qUnion([Q0])});
            skLineSegment(sketch, "E72", {"start": v(0, 23.73) * mm, "end": v(0, 50.2) * mm});
            skPoint(sketch, "E72.endSnap0", {"position": v(0, 35.5) * mm});
            skLineSegment(sketch, "E73.bottom", {"start": v(-2, 35) * mm, "end": v(-6, 35) * mm});
            skLineSegment(sketch, "E73.top", {"start": v(-2, 39.5) * mm, "end": v(-6, 39.5) * mm});
            skLineSegment(sketch, "E73.left", {"start": v(-2, 35) * mm, "end": v(-2, 39.5) * mm});
            skLineSegment(sketch, "E73.right", {"start": v(-6, 35) * mm, "end": v(-6, 39.5) * mm});
            skLineSegment(sketch, "E74.MirrorCS", {"start": v(2, 39.5) * mm, "end": v(6, 39.5) * mm});
            skLineSegment(sketch, "E75.MirrorCS", {"start": v(2, 35) * mm, "end": v(2, 39.5) * mm});
            skLineSegment(sketch, "E76.MirrorCS", {"start": v(2, 35) * mm, "end": v(6, 35) * mm});
            skLineSegment(sketch, "E77.MirrorCS", {"start": v(6, 35) * mm, "end": v(6, 39.5) * mm});
            skSolve(sketch);
        }
        {
            var Q0;
            Q0=qSketchRegion(id+"F47",true);
            extrude(context, id + "F48", {"entities" : qUnion([Q0]), "operationType" : NewBodyOperationType.REMOVE, "oppositeDirection" : true, "depth" : 4 * mm});
        }
        {
            var Q0;
            Q0=makeQuery(id+"F48.boolean.opBoolean","COPY",EDGE,{"derivedFrom":makeQuery(id+"F48.opExtrude","CAP_EDGE",EDGE,{"disambiguationData":[OSD([sQuery(id+"F47.wireOp",EDGE,"E76.MirrorCS")])],"isStart":true})});
            var Q1;
            Q1=makeQuery(id+"F48.boolean.opBoolean","INTERSECT",EDGE,{"derivedFrom":[makeQuery(id+"F11.opFillet","BLEND_FACE",FACE,{"disambiguationData":[OSD([sQuery(id+"F0.wireOp",EDGE,"E0.top")])]}),makeQuery(id+"F48.opExtrude","SWEPT_FACE",FACE,{"disambiguationData":[OSD([sQuery(id+"F47.wireOp",EDGE,"E75.MirrorCS")])]})]});
            var Q2;
            Q2=makeQuery(id+"F48.boolean.opBoolean","INTERSECT",EDGE,{"derivedFrom":[makeQuery(id+"F1.opExtrude","SWEPT_FACE",FACE,{"disambiguationData":[OSD([sQuery(id+"F0.wireOp",EDGE,"E0.top")])]}),makeQuery(id+"F48.opExtrude","CAP_FACE",FACE,{"disambiguationData":[OSD([sQuery(id+"F47.wireOp",EDGE,"E74.MirrorCS"),sQuery(id+"F47.wireOp",EDGE,"E75.MirrorCS"),sQuery(id+"F47.wireOp",EDGE,"E76.MirrorCS"),sQuery(id+"F47.wireOp",EDGE,"E77.MirrorCS")])],"isStart":false})]});
            var Q3;
            Q3=makeQuery(id+"F48.boolean.opBoolean","INTERSECT",EDGE,{"derivedFrom":[makeQuery(id+"F11.opFillet","BLEND_FACE",FACE,{"disambiguationData":[OSD([sQuery(id+"F0.wireOp",EDGE,"E0.top")])]}),makeQuery(id+"F48.opExtrude","SWEPT_FACE",FACE,{"disambiguationData":[OSD([sQuery(id+"F47.wireOp",EDGE,"E77.MirrorCS")])]})]});
            var Q4;
            Q4=makeQuery(id+"F48.boolean.opBoolean","COPY",EDGE,{"derivedFrom":makeQuery(id+"F48.opExtrude","CAP_EDGE",EDGE,{"disambiguationData":[OSD([sQuery(id+"F47.wireOp",EDGE,"E73.bottom")])],"isStart":true})});
            var Q5;
            Q5=makeQuery(id+"F48.boolean.opBoolean","INTERSECT",EDGE,{"derivedFrom":[makeQuery(id+"F11.opFillet","BLEND_FACE",FACE,{"disambiguationData":[OSD([sQuery(id+"F0.wireOp",EDGE,"E0.top")])]}),makeQuery(id+"F48.opExtrude","SWEPT_FACE",FACE,{"disambiguationData":[OSD([sQuery(id+"F47.wireOp",EDGE,"E73.left")])]})]});
            var Q6;
            Q6=makeQuery(id+"F48.boolean.opBoolean","INTERSECT",EDGE,{"derivedFrom":[makeQuery(id+"F11.opFillet","BLEND_FACE",FACE,{"disambiguationData":[OSD([sQuery(id+"F0.wireOp",EDGE,"E0.top")])]}),makeQuery(id+"F48.opExtrude","SWEPT_FACE",FACE,{"disambiguationData":[OSD([sQuery(id+"F47.wireOp",EDGE,"E73.right")])]})]});
            var Q7;
            Q7=makeQuery(id+"F48.boolean.opBoolean","INTERSECT",EDGE,{"derivedFrom":[makeQuery(id+"F1.opExtrude","SWEPT_FACE",FACE,{"disambiguationData":[OSD([sQuery(id+"F0.wireOp",EDGE,"E0.top")])]}),makeQuery(id+"F48.opExtrude","CAP_FACE",FACE,{"disambiguationData":[OSD([sQuery(id+"F47.wireOp",EDGE,"E73.bottom"),sQuery(id+"F47.wireOp",EDGE,"E73.top"),sQuery(id+"F47.wireOp",EDGE,"E73.left"),sQuery(id+"F47.wireOp",EDGE,"E73.right")])],"isStart":false})]});
            var Q8;
            {var subQ0=sQuery(id+"F0.wireOp",EDGE,"E0.bottom");var subQ1=sQuery(id+"F0.wireOp",EDGE,"E0.right");var subQ2=sQuery(id+"F0.wireOp",EDGE,"E0.left");var subQ3=sQuery(id+"F0.wireOp",EDGE,"E0.top");Q8=makeQuery(id+"F48.boolean.opBoolean","INTERSECT",EDGE,{"derivedFrom":[makeQuery(id+"FilWaYNq1lByzmx_5.boolean.opBoolean","SPLIT",FACE,{"disambiguationData":[TD([makeQuery(id+"F10.opFillet","BLEND_FACE",FACE,{"disambiguationData":[OSD([subQ3])]})])],"derivedFrom":makeQuery(id+"F4.opShell","OFFSET_FACE",FACE,{"disambiguationData":[OSD([subQ0,subQ3,subQ2,subQ1])]})}),makeQuery(id+"F48.opExtrude","SWEPT_FACE",FACE,{"disambiguationData":[OSD([sQuery(id+"F47.wireOp",EDGE,"E73.bottom")])]})]});}
            var Q9;
            Q9=makeQuery(id+"F48.boolean.opBoolean","INTERSECT",EDGE,{"derivedFrom":[makeQuery(id+"F10.opFillet","BLEND_FACE",FACE,{"disambiguationData":[OSD([sQuery(id+"F0.wireOp",EDGE,"E0.top")])]}),makeQuery(id+"F48.opExtrude","SWEPT_FACE",FACE,{"disambiguationData":[OSD([sQuery(id+"F47.wireOp",EDGE,"E73.right")])]})]});
            var Q10;
            Q10=makeQuery(id+"F48.boolean.opBoolean","INTERSECT",EDGE,{"derivedFrom":[makeQuery(id+"F10.opFillet","BLEND_FACE",FACE,{"disambiguationData":[OSD([sQuery(id+"F0.wireOp",EDGE,"E0.top")])]}),makeQuery(id+"F48.opExtrude","SWEPT_FACE",FACE,{"disambiguationData":[OSD([sQuery(id+"F47.wireOp",EDGE,"E73.left")])]})]});
            var Q11;
            Q11=makeQuery(id+"F48.boolean.opBoolean","INTERSECT",EDGE,{"derivedFrom":[makeQuery(id+"F4.opShell","OFFSET_FACE",FACE,{"disambiguationData":[OSD([sQuery(id+"F0.wireOp",EDGE,"E0.top")])]}),makeQuery(id+"F48.opExtrude","CAP_FACE",FACE,{"disambiguationData":[OSD([sQuery(id+"F47.wireOp",EDGE,"E73.bottom"),sQuery(id+"F47.wireOp",EDGE,"E73.top"),sQuery(id+"F47.wireOp",EDGE,"E73.left"),sQuery(id+"F47.wireOp",EDGE,"E73.right")])],"isStart":false})]});
            var Q12;
            {var subQ0=sQuery(id+"F0.wireOp",EDGE,"E0.bottom");var subQ1=sQuery(id+"F0.wireOp",EDGE,"E0.right");var subQ2=sQuery(id+"F0.wireOp",EDGE,"E0.left");var subQ3=sQuery(id+"F0.wireOp",EDGE,"E0.top");Q12=makeQuery(id+"F48.boolean.opBoolean","INTERSECT",EDGE,{"derivedFrom":[makeQuery(id+"FilWaYNq1lByzmx_5.boolean.opBoolean","SPLIT",FACE,{"disambiguationData":[TD([makeQuery(id+"F10.opFillet","BLEND_FACE",FACE,{"disambiguationData":[OSD([subQ3])]})])],"derivedFrom":makeQuery(id+"F4.opShell","OFFSET_FACE",FACE,{"disambiguationData":[OSD([subQ0,subQ3,subQ2,subQ1])]})}),makeQuery(id+"F48.opExtrude","SWEPT_FACE",FACE,{"disambiguationData":[OSD([sQuery(id+"F47.wireOp",EDGE,"E76.MirrorCS")])]})]});}
            var Q13;
            Q13=makeQuery(id+"F48.boolean.opBoolean","INTERSECT",EDGE,{"derivedFrom":[makeQuery(id+"F10.opFillet","BLEND_FACE",FACE,{"disambiguationData":[OSD([sQuery(id+"F0.wireOp",EDGE,"E0.top")])]}),makeQuery(id+"F48.opExtrude","SWEPT_FACE",FACE,{"disambiguationData":[OSD([sQuery(id+"F47.wireOp",EDGE,"E75.MirrorCS")])]})]});
            var Q14;
            Q14=makeQuery(id+"F48.boolean.opBoolean","INTERSECT",EDGE,{"derivedFrom":[makeQuery(id+"F10.opFillet","BLEND_FACE",FACE,{"disambiguationData":[OSD([sQuery(id+"F0.wireOp",EDGE,"E0.top")])]}),makeQuery(id+"F48.opExtrude","SWEPT_FACE",FACE,{"disambiguationData":[OSD([sQuery(id+"F47.wireOp",EDGE,"E77.MirrorCS")])]})]});
            var Q15;
            Q15=makeQuery(id+"F48.boolean.opBoolean","INTERSECT",EDGE,{"derivedFrom":[makeQuery(id+"F4.opShell","OFFSET_FACE",FACE,{"disambiguationData":[OSD([sQuery(id+"F0.wireOp",EDGE,"E0.top")])]}),makeQuery(id+"F48.opExtrude","CAP_FACE",FACE,{"disambiguationData":[OSD([sQuery(id+"F47.wireOp",EDGE,"E74.MirrorCS"),sQuery(id+"F47.wireOp",EDGE,"E75.MirrorCS"),sQuery(id+"F47.wireOp",EDGE,"E76.MirrorCS"),sQuery(id+"F47.wireOp",EDGE,"E77.MirrorCS")])],"isStart":false})]});
            fillet(context, id + "F49", {"entities" : qUnion([Q0, Q1, Q2, Q3, Q4, Q5, Q6, Q7, Q8, Q9, Q10, Q11, Q12, Q13, Q14, Q15]), "radius" : 0.5 * mm, "tangentPropagation" : true, "allowEdgeOverflow" : false});
        }
        {
            var Q0;
            Q0=makeQuery(id+"F1.opExtrude","CAP_FACE",FACE,{"disambiguationData":[OSD([sQuery(id+"F0.wireOp",EDGE,"E0.bottom"),sQuery(id+"F0.wireOp",EDGE,"E0.top"),sQuery(id+"F0.wireOp",EDGE,"E0.left"),sQuery(id+"F0.wireOp",EDGE,"E0.right")])],"isStart":false});
            var sketch = newSketch(context, id + "F50", { "sketchPlane" : qUnion([Q0])});
            skLineSegment(sketch, "E78", {"start": v(-26, 49.41) * mm, "end": v(-26, 10.8) * mm, "construction": true});
            skSolve(sketch);
        }
        {
            var Q0;
            Q0=qBodyType(qCreatedBy(id+"F50",EDGE),BodyType.WIRE);
            cPlane(context, id + "F51", {"entities" : qUnion([Q0]), "cplaneType" : CPlaneType.LINE_ANGLE, "offset" : 25 * mm, "angle" : 90 * degree, "width" : 150 * mm, "height" : 150 * mm});
        }
        {
            var Q0;
            Q0=makeQuery(id+"F1.opExtrude","SWEPT_FACE",FACE,{"disambiguationData":[OSD([sQuery(id+"F0.wireOp",EDGE,"E0.bottom")])]});
            var sketch = newSketch(context, id + "F52", { "sketchPlane" : qUnion([Q0])});
            skPoint(sketch, "E79.0", {"position": v(26, 7.6) * mm});
            skLineSegment(sketch, "E80.bottom", {"start": v(19.5, 8.18) * mm, "end": v(32.5, 8.18) * mm});
            skLineSegment(sketch, "E80.top", {"start": v(19.5, 4.8) * mm, "end": v(32.5, 4.8) * mm});
            skLineSegment(sketch, "E80.left", {"start": v(19.5, 8.18) * mm, "end": v(19.5, 4.8) * mm});
            skLineSegment(sketch, "E80.right", {"start": v(32.5, 8.18) * mm, "end": v(32.5, 4.8) * mm});
            skPoint(sketch, "E81", {"position": v(26, 8.18) * mm});
            skLineSegment(sketch, "E82", {"start": v(26, 7.6) * mm, "end": v(26, 8.9) * mm, "construction": true});
            skLineSegment(sketch, "E83", {"start": v(26.51, 8.8) * mm, "end": v(29.8, 8.8) * mm, "construction": true});
            skSolve(sketch);
        }
        {
            var Q0;
            Q0=qSketchRegion(id+"F52",true);
            extrude(context, id + "F53", {"entities" : qUnion([Q0]), "operationType" : NewBodyOperationType.REMOVE, "oppositeDirection" : true, "depth" : 0.6 * mm});
        }
        {
            var Q0;
            Q0=makeQuery(id+"F1.opExtrude","SWEPT_FACE",FACE,{"disambiguationData":[OSD([sQuery(id+"F0.wireOp",EDGE,"E0.bottom")])]});
            var sketch = newSketch(context, id + "F54", { "sketchPlane" : qUnion([Q0])});
            skLineSegment(sketch, "E84.bottom", {"start": v(22, 9) * mm, "end": v(30, 9) * mm});
            skPoint(sketch, "E85.0", {"position": v(26, 7.6) * mm});
            skLineSegment(sketch, "E86", {"start": v(26, 7.6) * mm, "end": v(26, 11.52) * mm, "construction": true});
            skPoint(sketch, "E87", {"position": v(26, 9) * mm});
            skLineSegment(sketch, "E88", {"start": v(22, 9) * mm, "end": v(22.5, 7) * mm});
            skLineSegment(sketch, "E89", {"start": v(22.5, 7) * mm, "end": v(29.5, 7) * mm});
            skLineSegment(sketch, "E90", {"start": v(29.5, 7) * mm, "end": v(30, 9) * mm});
            skPoint(sketch, "E91", {"position": v(26, 7) * mm});
            skSolve(sketch);
        }
        {
            var Q0;
            Q0=qSketchRegion(id+"F54",true);
            extrude(context, id + "F55", {"entities" : qUnion([Q0]), "operationType" : NewBodyOperationType.REMOVE, "oppositeDirection" : true, "depth" : 25 * mm});
        }
        {
            var Q0;
            Q0=qCreatedBy(id+"F51.planeOp",FACE);
            var sketch = newSketch(context, id + "F56", { "sketchPlane" : qUnion([Q0])});
            skLineSegment(sketch, "E92", {"start": v(35.23, 15.56) * mm, "end": v(33.1, 15.33) * mm});
            skLineSegment(sketch, "E93", {"start": v(33.1, 15.33) * mm, "end": v(33.89, 10.85) * mm});
            skLineSegment(sketch, "E94", {"start": v(33.89, 10.85) * mm, "end": v(36, 11.22) * mm});
            skLineSegment(sketch, "E95", {"start": v(36, 11.22) * mm, "end": v(35.23, 15.56) * mm});
            skLineSegment(sketch, "E96", {"start": v(36.6, 11.33) * mm, "end": v(33.04, 10.7) * mm, "construction": true});
            skSolve(sketch);
        }
        {
            var Q0;
            Q0=qSketchRegion(id+"F56",true);
            extrude(context, id + "F57", {"entities" : qUnion([Q0]), "operationType" : NewBodyOperationType.REMOVE, "endBound" : BoundingType.SYMMETRIC, "depth" : 12 * mm});
        }
        {
            var Q0;
            Q0=makeQuery(id+"F4.opShell","OFFSET_FACE",FACE,{"disambiguationData":[OSD([sQuery(id+"F0.wireOp",EDGE,"E0.bottom"),sQuery(id+"F0.wireOp",EDGE,"E0.top"),sQuery(id+"F0.wireOp",EDGE,"E0.left"),sQuery(id+"F0.wireOp",EDGE,"E0.right")])]});
            var sketch = newSketch(context, id + "F58", { "sketchPlane" : qUnion([Q0])});
            skLineSegment(sketch, "E97.bottom", {"start": v(13, 37) * mm, "end": v(-13, 37) * mm});
            skLineSegment(sketch, "E97.top", {"start": v(13, -6) * mm, "end": v(-13, -6) * mm});
            skLineSegment(sketch, "E97.left", {"start": v(13, 37) * mm, "end": v(13, -6) * mm});
            skLineSegment(sketch, "E97.right", {"start": v(-13, 37) * mm, "end": v(-13, -6) * mm});
            skPoint(sketch, "E97.middle", {"position": v(0, 15.5) * mm});
            skSolve(sketch);
        }
        {
            var Q0;
            {var subQ59=sQuery(id+"F58.wireOp",EDGE,"E97.top");Q0=makeQuery(id+"F58.imprint","IMPRINT",FACE,{"disambiguationData":[TD([[makeQuery(id+"F58.imprint","IMPRINT",EDGE,{"derivedFrom":subQ59}),1.0]])]});}
            var sketch = newSketch(context, id + "F59", { "sketchPlane" : qUnion([Q0])});
            skCircle(sketch, "E98", {"center": v(-8, 4) * mm, "radius": 4 * mm});
            skSolve(sketch);
        }
        {
            var Q0;
            Q0=qSketchRegion(id+"F59",true);
            extrude(context, id + "F60", {"entities" : qUnion([Q0]), "operationType" : NewBodyOperationType.ADD, "depth" : 0.1 * mm});
        }
        {
            var Q0;
            Q0=makeQuery(id+"F60.opExtrude","CAP_FACE",FACE,{"disambiguationData":[OSD([sQuery(id+"F59.wireOp",EDGE,"E98")])],"isStart":false});
            var sketch = newSketch(context, id + "F61", { "sketchPlane" : qUnion([Q0])});
            skCircle(sketch, "E99", {"center": v(-8, 4) * mm, "radius": 1.77 * mm});
            skSolve(sketch);
        }
        {
            var Q0;
            Q0=qSketchRegion(id+"F61",true);
            var Q1;
            Q1=makeQuery(id+"F1.opExtrude","CAP_FACE",FACE,{"disambiguationData":[OSD([sQuery(id+"F0.wireOp",EDGE,"E0.bottom"),sQuery(id+"F0.wireOp",EDGE,"E0.top"),sQuery(id+"F0.wireOp",EDGE,"E0.left"),sQuery(id+"F0.wireOp",EDGE,"E0.right")])],"isStart":true});
            extrude(context, id + "F62", {"entities" : qUnion([Q0]), "operationType" : NewBodyOperationType.REMOVE, "endBound" : BoundingType.UP_TO_SURFACE, "oppositeDirection" : true, "endBoundEntityFace" : qUnion([Q1]), "depth" : 25 * mm});
        }
    });
